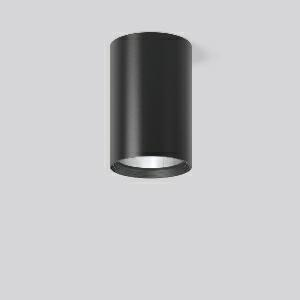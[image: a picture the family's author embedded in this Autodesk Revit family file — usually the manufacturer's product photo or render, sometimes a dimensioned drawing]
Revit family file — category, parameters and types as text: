
# Revit family: heledon_maxi_a_931225_003_76_f244
name_source: partatom
category: Lighting Fixtures
units: mm (PartAtom-declared; Revit-internal decimal feet)

## family parameters
Cut with Voids When Loaded = No
Host = Face
Light Source = No
Part Type = Normal
Room Calculation Point = No
Round Connector Dimension = Use Diameter
Shared = No

## types (1)
- HELEDON maxi A (1 x LED Modul 930, 4350 lm, 3000)
    Apparent Load = 35 VA
    Approval mark = CE
    CIE Flux Codes = 100 100 100 100 100
    Color Rendering = 90
    Color Temperature = 3000
    Default Elevation = 1800 mm
    Description = Series: HELEDON maxi
Cylindrical surface-mounted downlight. Housing: die-cast aluminium, powder-coated. Internal ceiling frame polycarbonate with bayonet mounting. Black plastic ring and recessed LED to prevent glare from the side. Optical assembly with reflector made of MIRO-Silver with 98% total light reflection for outstanding efficiency - can be changed without tools. Best colour rendering index Ra>90. Suitable for Ceiling mounting. Easy installation with a separate ceiling frame with bayonet mounting and plug connection. Driver integrated. Connected via plug-in connector. High quality converter without flickering and stroboscopic effect. The following accessories can be mounted without use of tools: interchangeable lenses, decorative glasses, honeycomb louvre, clear and frosted diffusers, white interchangeable plastic ring. 
Colour: deep black, matt (RAL 9005)
Diameter: 123 mm
Height: 183 mm
Lamp: LED
Socket: without socket
Colour temperature: 3000K
Colour rendering index (CRI): 92
System power: 35 W
Rated luminous flux: 4350 lm
Luminous efficiency: 124 lm/W
Control gear: Converter, dimmable, DALI
Protection class: I
Type of protection: IP 20
    Height = 183 mm
    Lamp = 1 x LED Modul 930
    Lamp Light Flux = 4350 lm
    Lamp count = 1
    Length = 123 mm
    Lifetime = 50000 h
    Luminous efficacy = 124 lm/W
    Manufacturer = RZB
    ModVariant = No
    Model = 931225.003.76
    Mounting Place = Ceiling
    Mounting Type = Surface mounted
    Number of Poles = 1
    OnlyDefault = Yes
    Power Factor = 1
    Product Name = HELEDON maxi A
    Product group = Surface mounted downlights
    ProductGroupID = 302
    Protection Class = Protection class I
    Protection Degree = IP 20
    RLX_Detail_Level = 1
    RLX_Emergency_Light_Flux = 0 lm
    RLX_Emergency_Type = 0
    RLX_Emergency_Type_DB = No
    RlxData = <blob elided: 95845 chars, md5=c4e08a07>
    Socket = socket
    Standby Power = 0 W
    System Light Flux = 4350 lm
    System Power = 35 W
    Type Comments = Product without accessories
    Type Image = 931192.003.jpg
    URL = http://relux.com
    VarID = ---
    Voltage = 230 V
    Voltage Range = 220-240 V
    Weight = 0.00 kg
    Width = 0 mm  [stored 0 ft]

note: [stored X ft] marks values corroborated as IEEE doubles in the binary element streams (Revit-internal decimal feet)

## geometry (parser evidence)
native form markers: Blend x4, Sweep x10
no freeform markers — native parametric forms only
